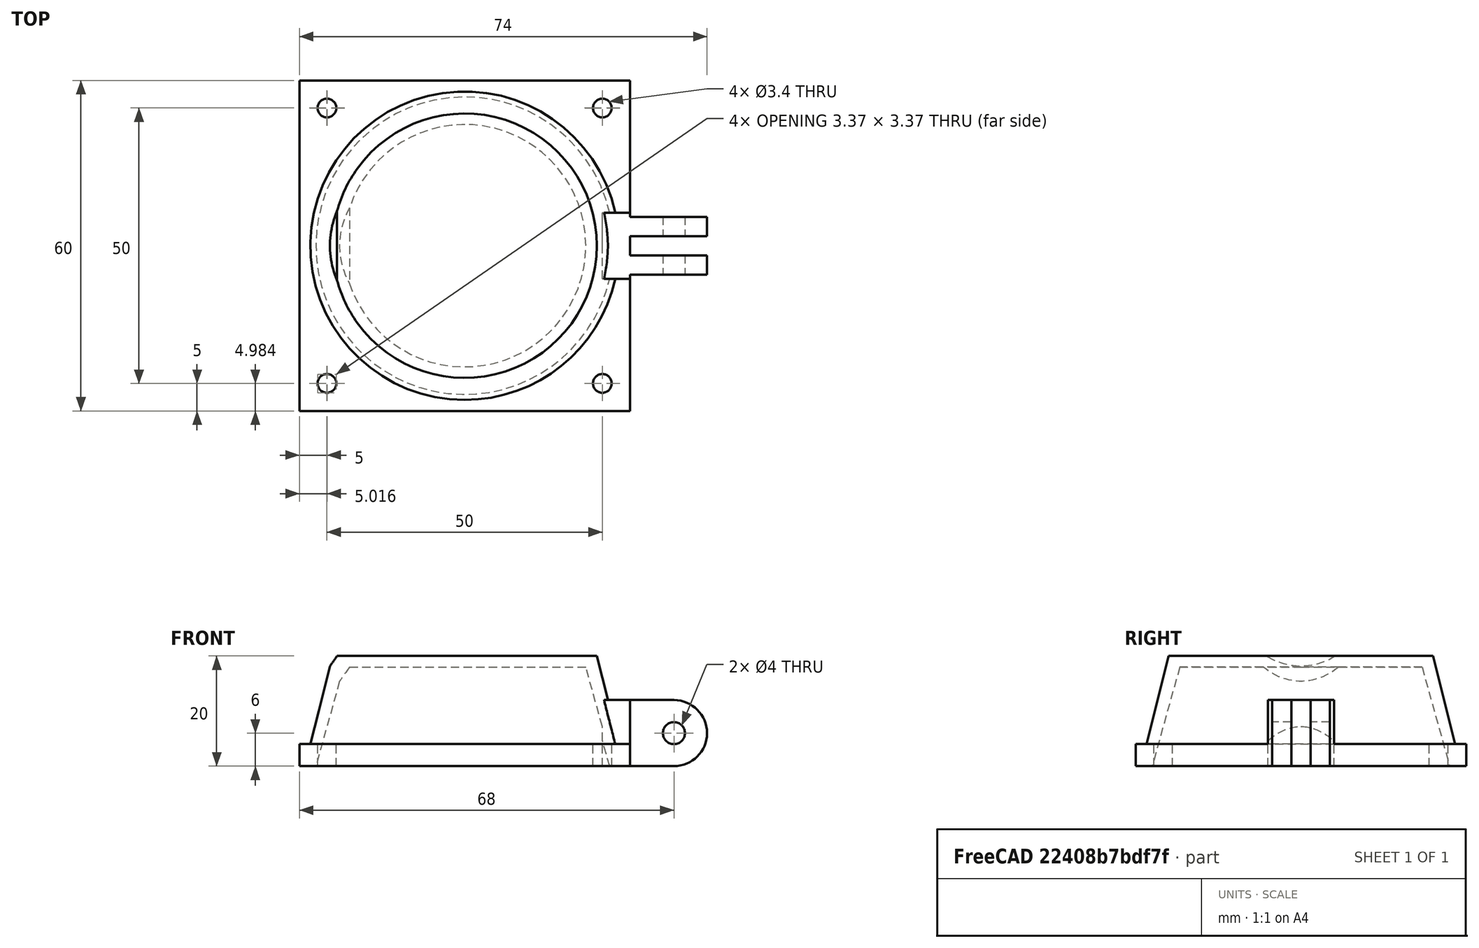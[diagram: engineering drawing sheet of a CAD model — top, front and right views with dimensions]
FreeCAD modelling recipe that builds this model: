
FCSTD DOCUMENT
Label: Fan_duct_4
objects: Part::Cut×8, Part::Cylinder×6, Part::Fuse×6, Part::Box×5, Part::Cone×3, Mesh::Feature×1, Part::Common×1, App::MeasureDistance×1
note: 29 computed .brp shape members not serialized (recipe doc carries the construction recipe); baked Part::Feature solids carry a one-line shape summary decoded from their .brp

FEATURE [Mesh::Feature] fan_mount_fan
  Placement = pos=(-47,21,0) rot=(0,0,1;0rad)
FEATURE [Part::Box] Box
  Height = 4
  Length = 60
  Width = 60
FEATURE [Part::Cylinder] Cylinder
  Angle = 360
  Height = 10
  Placement = pos=(5,5,-4) rot=(0,0,1;0rad)
  Radius = 1.7
FEATURE [Part::Cylinder] Cylinder001
  Angle = 360
  Height = 10
  Placement = pos=(55,5,-4) rot=(0,0,1;0rad)
  Radius = 1.7
FEATURE [Part::Cylinder] Cylinder002
  Angle = 360
  Height = 10
  Placement = pos=(5,55,-4) rot=(0,0,1;0rad)
  Radius = 1.7
FEATURE [Part::Cylinder] Cylinder002001
  Angle = 360
  Height = 10
  Placement = pos=(55,55,-4) rot=(0,0,1;0rad)
  Radius = 1.7
FEATURE [Part::Cut] Cut
  Base = -> Box
  Tool = -> Cylinder
FEATURE [Part::Cut] Cut001
  Base = -> Cut
  Tool = -> Cylinder001
FEATURE [Part::Cut] Cut002
  Base = -> Cut001
  Tool = -> Cylinder002
FEATURE [Part::Cut] Cut003  label="Base1"
  Base = -> Cut002
  Tool = -> Cylinder002001
FEATURE [Part::Cone] Cone  label="Corps du duct"
  Angle = 360
  Height = 20
  Placement = pos=(30,30,0) rot=(0,0,1;0rad)
  Radius1 = 29
  Radius2 = 24
FEATURE [Part::Cone] Cone001  label="Trou principal"
  Angle = 360
  Height = 18
  Placement = pos=(30,30,0) rot=(0,0,1;0rad)
  Radius1 = 27
  Radius2 = 22
FEATURE [Part::Box] Box001
  Height = 3
  Length = 60
  Placement = pos=(0,0,5) rot=(0,-1,0;0.959932rad)
  Width = 60
FEATURE [Part::Cone] Cone002
  Angle = 360
  Height = 20
  Placement = pos=(30,30,0) rot=(0,0,1;0rad)
  Radius1 = 29
  Radius2 = 24
FEATURE [Part::Common] Common  label="Meplat"
  Base = -> Box001
  Tool = -> Cone002
FEATURE [Part::Box] Box001001  label="A retirer pour meplat"
  Height = 24
  Length = 60
  Placement = pos=(0,0,5) rot=(0,-1,0;0.959932rad)
  Width = 60
FEATURE [Part::Fuse] Fusion  label="Base2"
  Base = -> Cut003
  Tool = -> Cone
FEATURE [Part::Cut] Cut004  label="Base3"
  Base = -> Fusion
  Tool = -> Cone001
FEATURE [Part::Cut] Cut005  label="Base4"
  Base = -> Cut004
  Tool = -> Box001001
FEATURE [Part::Fuse] Fusion001  label="Base5"
  Base = -> Cut005
  Tool = -> Common
FEATURE [Part::Cylinder] Cylinder002002
  Angle = 360
  Height = 3.5
  Placement = pos=(68,28.25,6) rot=(1,0,0;1.5708rad)
  Radius = 6
FEATURE [Part::Cylinder] Cylinder002002001
  Angle = 360
  Height = 4.8
  Placement = pos=(68,29.25,6) rot=(1,0,0;1.5708rad)
  Radius = 2
FEATURE [Part::Box] Box001003  label="Plat languettes"
  Height = 12
  Length = 5
  Placement = pos=(55,24,0) rot=(0,0,1;0rad)
  Width = 12
FEATURE [Part::Box] Box001004
  Height = 12
  Length = 12
  Placement = pos=(56,24.75,0) rot=(0,0,1;0rad)
  Width = 3.5
FEATURE [Part::Fuse] Fusion002
  Base = -> Box001004
  Tool = -> Cylinder002002
FEATURE [Part::Cut] Cut006  label="Languette1"
  Base = -> Fusion002
  Tool = -> Cylinder002002001
FEATURE [Part::Cut] Cut006001  label="Languette002"
  Base = -> Fusion002
  Placement = pos=(0,7,0) rot=(0,0,1;0rad)
  Tool = -> Cylinder002002001
FEATURE [Part::Fuse] Fusion003
  Base = -> Box001003
  Tool = -> Cut006
FEATURE [Part::Fuse] Fusion004  label="Languette tot"
  Base = -> Fusion003
  Tool = -> Cut006001
FEATURE [Part::Fuse] Fusion005  label="Fan duct 4"
  Base = -> Fusion001
  Tool = -> Fusion004
FEATURE [App::MeasureDistance] Distance  label="Distance: 3.500"
  Distance = 3.5
  P1 = (60,31.75,12)
  P2 = (60,28.25,12)
